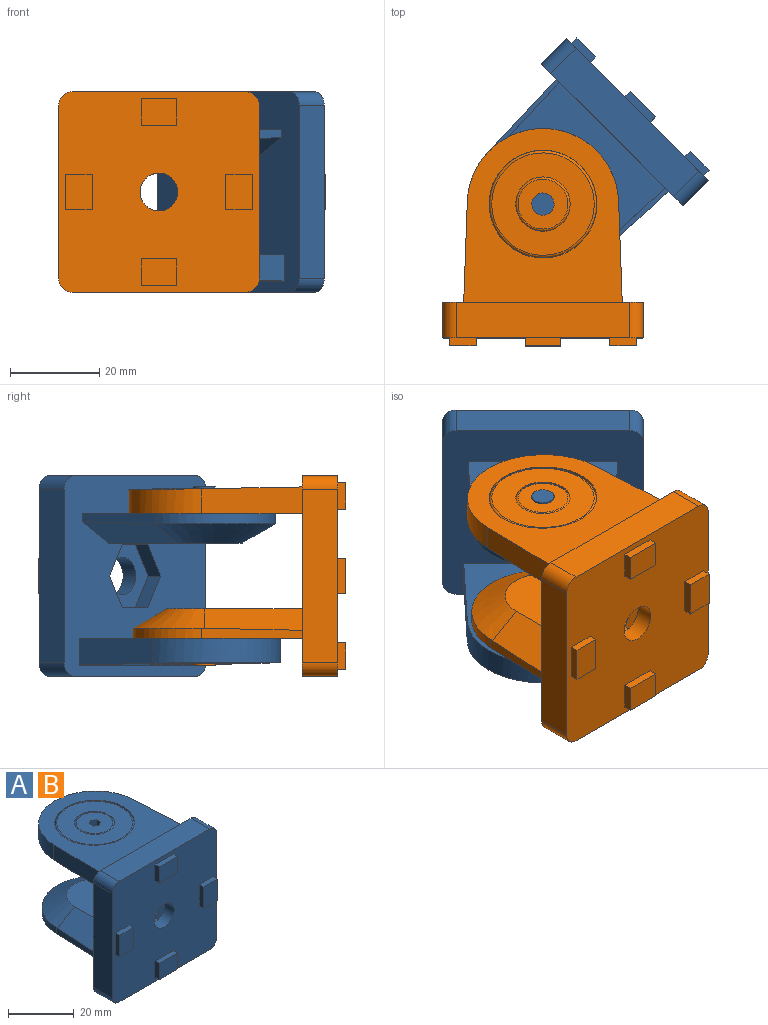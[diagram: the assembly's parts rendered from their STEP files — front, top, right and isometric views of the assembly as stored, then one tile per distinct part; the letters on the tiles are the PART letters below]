
ASSEMBLY  parts=2 mates=1
PART A: 70 faces, bbox 45.1x48.9x45.1 mm
  f0: plane 22.61x6mm, normal (1,0.04,0), area 131.3mm2, adj f12,f13,f17,f69
  f1: plane 30.5x17mm, normal (0,0,1), area 487.5mm2, adj f5,f6,f7,f13
  f2: plane 22.61x6mm, normal (-1,0.04,0), area 131.3mm2, adj f12,f13,f17,f69
  f3: plane 22.58x2.28mm, normal (-1,0.04,0), area 46.1mm2, adj f5,f6,f10,f11,f13
  f4: plane 22.58x2.28mm, normal (1,0.04,0), area 46.1mm2, adj f5,f7,f10,f11,f13
  f5: cone r=18.89mm half-angle=60deg, axis (0,0,-1), area 333.3mm2, adj f1,f3,f4,f6,f7,f11
  f6: plane 22x8.3mm, normal (-0.5,0,0.87), area 200.8mm2, adj f1,f3,f5,f13
  f7: plane 22x8.3mm, normal (0.5,0,0.87), area 200.8mm2, adj f1,f4,f5,f13
  f8: plane 5x5mm, normal (0,0,-1), area 19.6mm2, adj f9
  f9: cylinder r=2.5mm len=6mm, axis (0,0,1), area 94.2mm2, adj f8,f10
  f10: plane 38x33.6mm, normal (0,0,-1), area 1104.3mm2, adj f3,f4,f9,f11,f13
  f11: cylinder r=16mm len=31.98mm, axis (0,0,1), area 111.5mm2, adj f3,f4,f5,f10
  f12: plane 39.09x35.69mm, normal (0,0.02,1), area 760mm2, adj f0,f2,f13,f19,f69
  f13: plane 45x45mm, normal (0,1,0), area 1451.9mm2, adj f0,f1,f2,f3,f4,f6,f7,f10
  f14: plane 39x8mm, normal (-1,0,0), area 312mm2, adj f13,f22,f23,f28
  f15: cylinder r=4.25mm len=8.5mm, axis (0,1,0), area 106.8mm2, adj f28,f68
  f16: plane 39x8mm, normal (1,0,0), area 312mm2, adj f13,f25,f26,f28
  f17: plane 39x35.6mm, normal (0,0,-1), area 1200.2mm2, adj f0,f2,f13,f18,f69
  f18: cylinder r=2.5mm len=5mm, axis (0,0,1), area 15.7mm2, adj f17,f20
  f19: cylinder r=12.1mm len=24.2mm, axis (0,0,1), area 199.4mm2, adj f12,f21
  f20: plane 5x5mm, normal (0,0,-1), area 19.6mm2, adj f18
  f21: plane 24.2x24.2mm, normal (0,0,1), area 7.6mm2, adj f19,f54
  f22: cylinder r=3mm len=8mm, axis (0,1,0), area 37.7mm2, adj f13,f14,f27,f28
  f23: cylinder r=3mm len=8mm, axis (0,1,0), area 37.7mm2, adj f13,f14,f24,f28
  f24: plane 39x8mm, normal (0,0,1), area 312mm2, adj f13,f23,f25,f28
  f25: cylinder r=3mm len=8mm, axis (0,1,0), area 37.7mm2, adj f13,f16,f24,f28
  f26: cylinder r=3mm len=8mm, axis (0,1,0), area 37.7mm2, adj f13,f16,f27,f28
  f27: plane 39x8mm, normal (0,0,-1), area 312mm2, adj f13,f22,f26,f28
  f28: plane 45x45mm, normal (0,-1,0), area 1768.5mm2, adj f14,f15,f16,f22,f23,f24,f25,f26
  f29: plane 8x1.8mm, normal (-1,0,0), area 14.4mm2, adj f28,f30,f32,f33
  f30: plane 8x6mm, normal (0,-1,0), area 48mm2, adj f29,f31,f32,f33
  f31: plane 8x1.8mm, normal (1,0,0), area 14.4mm2, adj f28,f30,f32,f33
  f32: plane 6x1.8mm, normal (0,0,-1), area 10.8mm2, adj f28,f29,f30,f31
  f33: plane 6x1.8mm, normal (0,0,1), area 10.8mm2, adj f28,f29,f30,f31
  f34: plane 8x1.8mm, normal (-1,0,0), area 14.4mm2, adj f28,f35,f37,f38
  f35: plane 8x6mm, normal (0,-1,0), area 48mm2, adj f34,f36,f37,f38
  f36: plane 8x1.8mm, normal (1,0,0), area 14.4mm2, adj f28,f35,f37,f38
  f37: plane 6x1.8mm, normal (0,0,-1), area 10.8mm2, adj f28,f34,f35,f36
  f38: plane 6x1.8mm, normal (0,0,1), area 10.8mm2, adj f28,f34,f35,f36
  f39: plane 8x1.8mm, normal (0,0,1), area 14.4mm2, adj f28,f40,f42,f43
  f40: plane 8x6mm, normal (0,-1,0), area 48mm2, adj f39,f41,f42,f43
  f41: plane 8x1.8mm, normal (0,0,-1), area 14.4mm2, adj f28,f40,f42,f43
  f42: plane 6x1.8mm, normal (-1,0,0), area 10.8mm2, adj f28,f39,f40,f41
  f43: plane 6x1.8mm, normal (1,0,0), area 10.8mm2, adj f28,f39,f40,f41
  f44: plane 8x1.8mm, normal (0,0,1), area 14.4mm2, adj f28,f45,f47,f48
  f45: plane 8x6mm, normal (0,-1,0), area 48mm2, adj f44,f46,f47,f48
  f46: plane 8x1.8mm, normal (0,0,-1), area 14.4mm2, adj f28,f45,f47,f48
  f47: plane 6x1.8mm, normal (-1,0,0), area 10.8mm2, adj f28,f44,f45,f46
  f48: plane 6x1.8mm, normal (1,0,0), area 10.8mm2, adj f28,f44,f45,f46
  f49: plane 11.2x11.2mm, normal (0,0,1), area 90.7mm2, adj f50,f55,f56,f57,f58,f59,f60
  f50: torus R=5.6mm, axis (0,0,-1), area 29.2mm2, adj f49,f51
  f51: cylinder r=6.1mm len=12.2mm, axis (0,0,1), area 19.2mm2, adj f50,f52
  f52: plane 23x23mm, normal (0,0,1), area 298.6mm2, adj f51,f53
  f53: torus R=11.5mm, axis (0,0,-1), area 58.3mm2, adj f52,f54
  f54: cylinder r=12mm len=24mm, axis (0,0,1), area 154.6mm2, adj f21,f53
  f55: plane 3x1.73mm, normal (1,0,0), area 5.2mm2, adj f49,f56,f60,f61
  f56: plane 3x1.5mm, normal (0.5,0.87,0), area 5.2mm2, adj f49,f55,f57,f61
  f57: plane 3x1.5mm, normal (-0.5,0.87,0), area 5.2mm2, adj f49,f56,f58,f61
  f58: plane 3x1.73mm, normal (-1,0,0), area 5.2mm2, adj f49,f57,f59,f61
  f59: plane 3x1.5mm, normal (-0.5,-0.87,0), area 5.2mm2, adj f49,f58,f60,f61
  f60: plane 3x1.5mm, normal (0.5,-0.87,0), area 5.2mm2, adj f49,f55,f59,f61
  f61: plane 3.46x3mm, normal (0,0,1), area 7.8mm2, adj f55,f56,f57,f58,f59,f60
  f62: plane 7x4.04mm, normal (0.87,0,0.5), area 32.3mm2, adj f13,f63,f67,f68
  f63: plane 7x4.04mm, normal (0.87,0,-0.5), area 32.3mm2, adj f13,f62,f64,f68
  f64: plane 8.08x4mm, normal (0,0,-1), area 32.3mm2, adj f13,f63,f65,f68
  f65: plane 7x4.04mm, normal (-0.87,0,-0.5), area 32.3mm2, adj f13,f64,f66,f68
  f66: plane 7x4.04mm, normal (-0.87,0,0.5), area 32.3mm2, adj f13,f65,f67,f68
  f67: plane 8.08x4mm, normal (0,0,1), area 32.3mm2, adj f13,f62,f66,f68
  f68: plane 16.17x14mm, normal (0,1,0), area 113mm2, adj f15,f62,f63,f64,f65,f66,f67
  f69: cylinder r=17mm len=33.98mm, axis (0,0,1), area 283mm2, adj f0,f2,f12,f17
PART B: same geometry as A
PLACE A rot(axis=(0.92,-0.38,0),180deg) t=(0.31,30.09,0)mm
PLACE B t=(0.31,30.09,0)mm
MATE revolute B.f5 <-> A.f5  axis (0,0,-1) through (0.31,30.09,-14)mm
